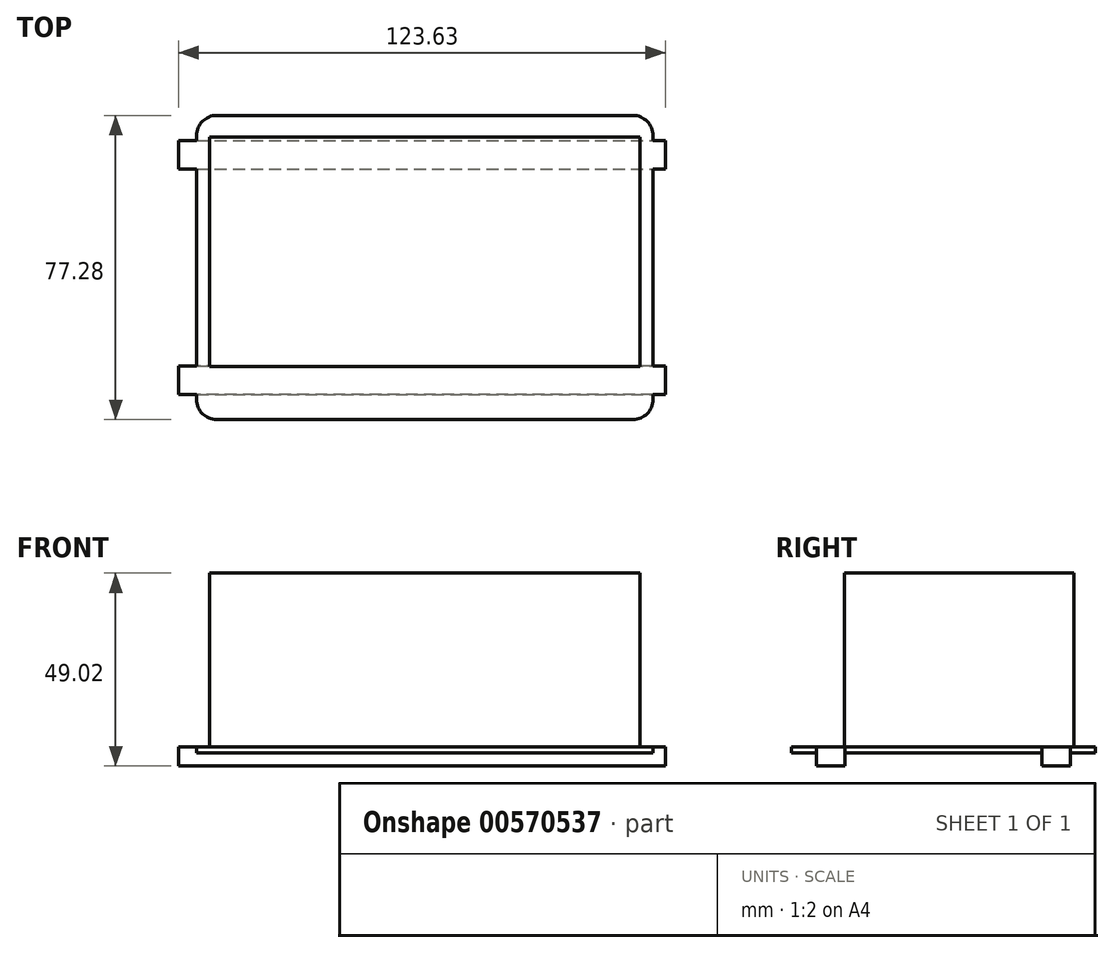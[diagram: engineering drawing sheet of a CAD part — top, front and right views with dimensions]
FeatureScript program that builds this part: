
annotation { "Feature Type Name" : "Feature", "Feature Type Description" : "" }
export const myFeature = defineFeature(function(context is Context, id is Id, definition is map)
    precondition{}
    {
        {
            var Q0;
            Q0=qCreatedBy(makeId("Top.planeOp"),FACE);
            var sketch = newSketch(context, id + "F0", { "sketchPlane" : qUnion([Q0])});
            skLineSegment(sketch, "E0.bottom", {"start": v(-64.1, -12.77) * mm, "end": v(59.53, -12.77) * mm});
            skLineSegment(sketch, "E0.top", {"start": v(-64.1, -20) * mm, "end": v(59.53, -20) * mm});
            skLineSegment(sketch, "E0.left", {"start": v(-64.1, -12.77) * mm, "end": v(-64.1, -20) * mm});
            skLineSegment(sketch, "E0.right", {"start": v(59.53, -12.77) * mm, "end": v(59.53, -20) * mm});
            skLineSegment(sketch, "E1", {"start": v(-74.95, 12.3) * mm, "end": v(105.56, 12.3) * mm, "construction": true});
            skLineSegment(sketch, "E2.MirrorCS", {"start": v(-64.1, 37.35) * mm, "end": v(59.53, 37.35) * mm});
            skLineSegment(sketch, "E3.MirrorCS", {"start": v(-64.1, 44.58) * mm, "end": v(59.53, 44.58) * mm});
            skLineSegment(sketch, "E4.MirrorCS", {"start": v(-64.1, 37.35) * mm, "end": v(-64.1, 44.58) * mm});
            skLineSegment(sketch, "E5.MirrorCS", {"start": v(59.53, 37.35) * mm, "end": v(59.53, 44.58) * mm});
            skSolve(sketch);
        }
        {
            var Q0;
            Q0 = qSketchRegion(id + "F0", true);
            extrude(context, id + "F1", {"entities" : qUnion([Q0]), "depth" : 4.83 * mm, "offsetDistance" : 25.4 * mm});
        }
        {
            var Q0;
            Q0=makeQuery(id+"F1.opExtrude","CAP_FACE",FACE,{"disambiguationData":[OSD([sQuery(id+"F0.wireOp",EDGE,"E2.MirrorCS"),sQuery(id+"F0.wireOp",EDGE,"E3.MirrorCS"),sQuery(id+"F0.wireOp",EDGE,"E4.MirrorCS"),sQuery(id+"F0.wireOp",EDGE,"E5.MirrorCS")])],"isStart":false});
            var sketch = newSketch(context, id + "F2", { "sketchPlane" : qUnion([Q0])});
            skLineSegment(sketch, "E6.bottom", {"start": v(-59.55, 50.93) * mm, "end": v(56.4, 50.93) * mm});
            skLineSegment(sketch, "E6.top", {"start": v(-59.55, -26.35) * mm, "end": v(56.4, -26.35) * mm});
            skLineSegment(sketch, "E6.left", {"start": v(-59.55, 50.93) * mm, "end": v(-59.55, -26.35) * mm});
            skLineSegment(sketch, "E6.right", {"start": v(56.4, 50.93) * mm, "end": v(56.4, -26.35) * mm});
            skSolve(sketch);
        }
        {
            var Q0;
            {var subQ0=sQuery(id+"F2.wireOp",EDGE,"E6.left");var subQ1=makeQuery(id+"F1.opExtrude","CAP_EDGE",EDGE,{"disambiguationData":[OSD([sQuery(id+"F0.wireOp",EDGE,"E3.MirrorCS")])],"isStart":false});var subQ2=makeQuery(id+"F2.imprint","INTERSECT",VERTEX,{"derivedFrom":[subQ1,subQ0]});Q0=makeQuery(id+"F2.imprint","IMPRINT",FACE,{"disambiguationData":[TD([[makeQuery(id+"F2.imprint","IMPRINT",EDGE,{"disambiguationData":[TD([[subQ2,-1.0]])],"derivedFrom":subQ0}),1.0]])]});}
            var Q1;
            {var subQ0=sQuery(id+"F2.wireOp",EDGE,"E6.bottom");Q1=makeQuery(id+"F2.imprint","IMPRINT",FACE,{"disambiguationData":[TD([[makeQuery(id+"F2.imprint","IMPRINT",EDGE,{"derivedFrom":subQ0}),-1.0]])]});}
            var Q2;
            {var subQ0=sQuery(id+"F2.wireOp",EDGE,"E6.top");Q2=makeQuery(id+"F2.imprint","IMPRINT",FACE,{"disambiguationData":[TD([[makeQuery(id+"F2.imprint","IMPRINT",EDGE,{"derivedFrom":subQ0}),1.0]])]});}
            extrude(context, id + "F3", {"entities" : qUnion([Q0, Q1, Q2]), "oppositeDirection" : true, "depth" : 1.52 * mm, "offsetDistance" : 25.4 * mm});
        }
        {
            var Q0;
            Q0=makeQuery(id+"F1.opExtrude","SWEPT_BODY",BODY,{"disambiguationData":[OSD([sQuery(id+"F0.wireOp",EDGE,"E2.MirrorCS"),sQuery(id+"F0.wireOp",EDGE,"E3.MirrorCS"),sQuery(id+"F0.wireOp",EDGE,"E4.MirrorCS"),sQuery(id+"F0.wireOp",EDGE,"E5.MirrorCS")])]});
            var Q1;
            Q1=makeQuery(id+"F3.opExtrude","SWEPT_BODY",BODY,{"disambiguationData":[OSD([sQuery(id+"F2.wireOp",EDGE,"E6.bottom"),sQuery(id+"F2.wireOp",EDGE,"E6.top"),sQuery(id+"F2.wireOp",EDGE,"E6.left"),sQuery(id+"F2.wireOp",EDGE,"E6.right")])]});
            var Q2;
            Q2=makeQuery(id+"F1.opExtrude","SWEPT_BODY",BODY,{"disambiguationData":[OSD([sQuery(id+"F0.wireOp",EDGE,"E0.bottom"),sQuery(id+"F0.wireOp",EDGE,"E0.top"),sQuery(id+"F0.wireOp",EDGE,"E0.left"),sQuery(id+"F0.wireOp",EDGE,"E0.right")])]});
            booleanBodies(context, id + "F4", {"operationType" : BooleanOperationType.UNION, "tools" : qUnion([Q0, Q1, Q2])});
        }
        {
            var Q0;
            Q0=makeQuery(id+"F3.opExtrude","SWEPT_EDGE",EDGE,{"disambiguationData":[OSD([sQuery(id+"F2.wireOp",EDGE,"E6.top"),sQuery(id+"F2.wireOp",EDGE,"E6.left")])]});
            var Q1;
            Q1=makeQuery(id+"F3.opExtrude","SWEPT_EDGE",EDGE,{"disambiguationData":[OSD([sQuery(id+"F2.wireOp",EDGE,"E6.top"),sQuery(id+"F2.wireOp",EDGE,"E6.right")])]});
            var Q2;
            Q2=makeQuery(id+"F3.opExtrude","SWEPT_EDGE",EDGE,{"disambiguationData":[OSD([sQuery(id+"F2.wireOp",EDGE,"E6.bottom"),sQuery(id+"F2.wireOp",EDGE,"E6.right")])]});
            var Q3;
            Q3=makeQuery(id+"F3.opExtrude","SWEPT_EDGE",EDGE,{"disambiguationData":[OSD([sQuery(id+"F2.wireOp",EDGE,"E6.bottom"),sQuery(id+"F2.wireOp",EDGE,"E6.left")])]});
            fillet(context, id + "F5", {"entities" : qUnion([Q0, Q1, Q2, Q3]), "radius" : 5.08 * mm, "tangentPropagation" : true, "allowEdgeOverflow" : false});
        }
        {
            var Q0;
            Q0=makeQuery(id+"F4.opBoolean","MERGE",FACE,{"derivedFrom":[makeQuery(id+"F1.opExtrude","CAP_FACE",FACE,{"disambiguationData":[OSD([sQuery(id+"F0.wireOp",EDGE,"E0.bottom"),sQuery(id+"F0.wireOp",EDGE,"E0.top"),sQuery(id+"F0.wireOp",EDGE,"E0.left"),sQuery(id+"F0.wireOp",EDGE,"E0.right")])],"isStart":false}),makeQuery(id+"F1.opExtrude","CAP_FACE",FACE,{"disambiguationData":[OSD([sQuery(id+"F0.wireOp",EDGE,"E2.MirrorCS"),sQuery(id+"F0.wireOp",EDGE,"E3.MirrorCS"),sQuery(id+"F0.wireOp",EDGE,"E4.MirrorCS"),sQuery(id+"F0.wireOp",EDGE,"E5.MirrorCS")])],"isStart":false}),makeQuery(id+"F3.opExtrude","CAP_FACE",FACE,{"disambiguationData":[OSD([sQuery(id+"F2.wireOp",EDGE,"E6.bottom"),sQuery(id+"F2.wireOp",EDGE,"E6.top"),sQuery(id+"F2.wireOp",EDGE,"E6.left"),sQuery(id+"F2.wireOp",EDGE,"E6.right")])],"isStart":true})]});
            var sketch = newSketch(context, id + "F6", { "sketchPlane" : qUnion([Q0])});
            skLineSegment(sketch, "E7.bottom", {"start": v(-56.25, 45.47) * mm, "end": v(-52.95, 45.47) * mm});
            skLineSegment(sketch, "E7.top", {"start": v(-56.25, -12.82) * mm, "end": v(-52.95, -12.82) * mm});
            skLineSegment(sketch, "E7.left", {"start": v(-56.25, 45.47) * mm, "end": v(-56.25, -12.82) * mm});
            skLineSegment(sketch, "E7.right", {"start": v(-52.95, 45.47) * mm, "end": v(-52.95, -12.82) * mm});
            skLineSegment(sketch, "E8.bottom", {"start": v(49.8, 45.47) * mm, "end": v(53.1, 45.47) * mm});
            skLineSegment(sketch, "E8.top", {"start": v(49.8, -12.82) * mm, "end": v(53.1, -12.82) * mm});
            skLineSegment(sketch, "E8.left", {"start": v(49.8, 45.47) * mm, "end": v(49.8, -12.82) * mm});
            skLineSegment(sketch, "E8.right", {"start": v(53.1, 45.47) * mm, "end": v(53.1, -12.82) * mm});
            skLineSegment(sketch, "E9.bottom", {"start": v(-52.95, 45.47) * mm, "end": v(49.8, 45.47) * mm});
            skLineSegment(sketch, "E9.top", {"start": v(-52.95, 42.07) * mm, "end": v(49.8, 42.07) * mm});
            skLineSegment(sketch, "E9.left", {"start": v(-52.95, 45.47) * mm, "end": v(-52.95, 42.07) * mm});
            skLineSegment(sketch, "E9.right", {"start": v(49.8, 45.47) * mm, "end": v(49.8, 42.07) * mm});
            skLineSegment(sketch, "E10.bottom", {"start": v(-52.95, -12.82) * mm, "end": v(49.8, -12.82) * mm});
            skLineSegment(sketch, "E10.top", {"start": v(-52.95, -9.42) * mm, "end": v(49.8, -9.42) * mm});
            skLineSegment(sketch, "E10.left", {"start": v(-52.95, -12.82) * mm, "end": v(-52.95, -9.42) * mm});
            skLineSegment(sketch, "E10.right", {"start": v(49.8, -12.82) * mm, "end": v(49.8, -9.42) * mm});
            skSolve(sketch);
        }
        {
            var Q0;
            Q0 = qSketchRegion(id + "F6", true);
            extrude(context, id + "F7", {"entities" : qUnion([Q0]), "operationType" : NewBodyOperationType.ADD, "depth" : 44.2 * mm, "offsetDistance" : 25.4 * mm});
        }
        {
            var Q0;
            Q0=makeQuery(id+"F7.boolean.opBoolean","SPLIT",FACE,{"disambiguationData":[TD([makeQuery(id+"F7.opExtrude","SWEPT_FACE",FACE,{"disambiguationData":[OSD([sQuery(id+"F6.wireOp",EDGE,"E7.right")])]})])],"derivedFrom":makeQuery(id+"F4.opBoolean","MERGE",FACE,{"derivedFrom":[makeQuery(id+"F1.opExtrude","CAP_FACE",FACE,{"disambiguationData":[OSD([sQuery(id+"F0.wireOp",EDGE,"E0.bottom"),sQuery(id+"F0.wireOp",EDGE,"E0.top"),sQuery(id+"F0.wireOp",EDGE,"E0.left"),sQuery(id+"F0.wireOp",EDGE,"E0.right")])],"isStart":false}),makeQuery(id+"F1.opExtrude","CAP_FACE",FACE,{"disambiguationData":[OSD([sQuery(id+"F0.wireOp",EDGE,"E2.MirrorCS"),sQuery(id+"F0.wireOp",EDGE,"E3.MirrorCS"),sQuery(id+"F0.wireOp",EDGE,"E4.MirrorCS"),sQuery(id+"F0.wireOp",EDGE,"E5.MirrorCS")])],"isStart":false}),makeQuery(id+"F3.opExtrude","CAP_FACE",FACE,{"disambiguationData":[OSD([sQuery(id+"F2.wireOp",EDGE,"E6.bottom"),sQuery(id+"F2.wireOp",EDGE,"E6.top"),sQuery(id+"F2.wireOp",EDGE,"E6.left"),sQuery(id+"F2.wireOp",EDGE,"E6.right")])],"isStart":true})]})});
            extrude(context, id + "F8", {"entities" : qUnion([Q0]), "operationType" : NewBodyOperationType.ADD, "depth" : 44.2 * mm, "offsetDistance" : 25.4 * mm});
        }
    });
